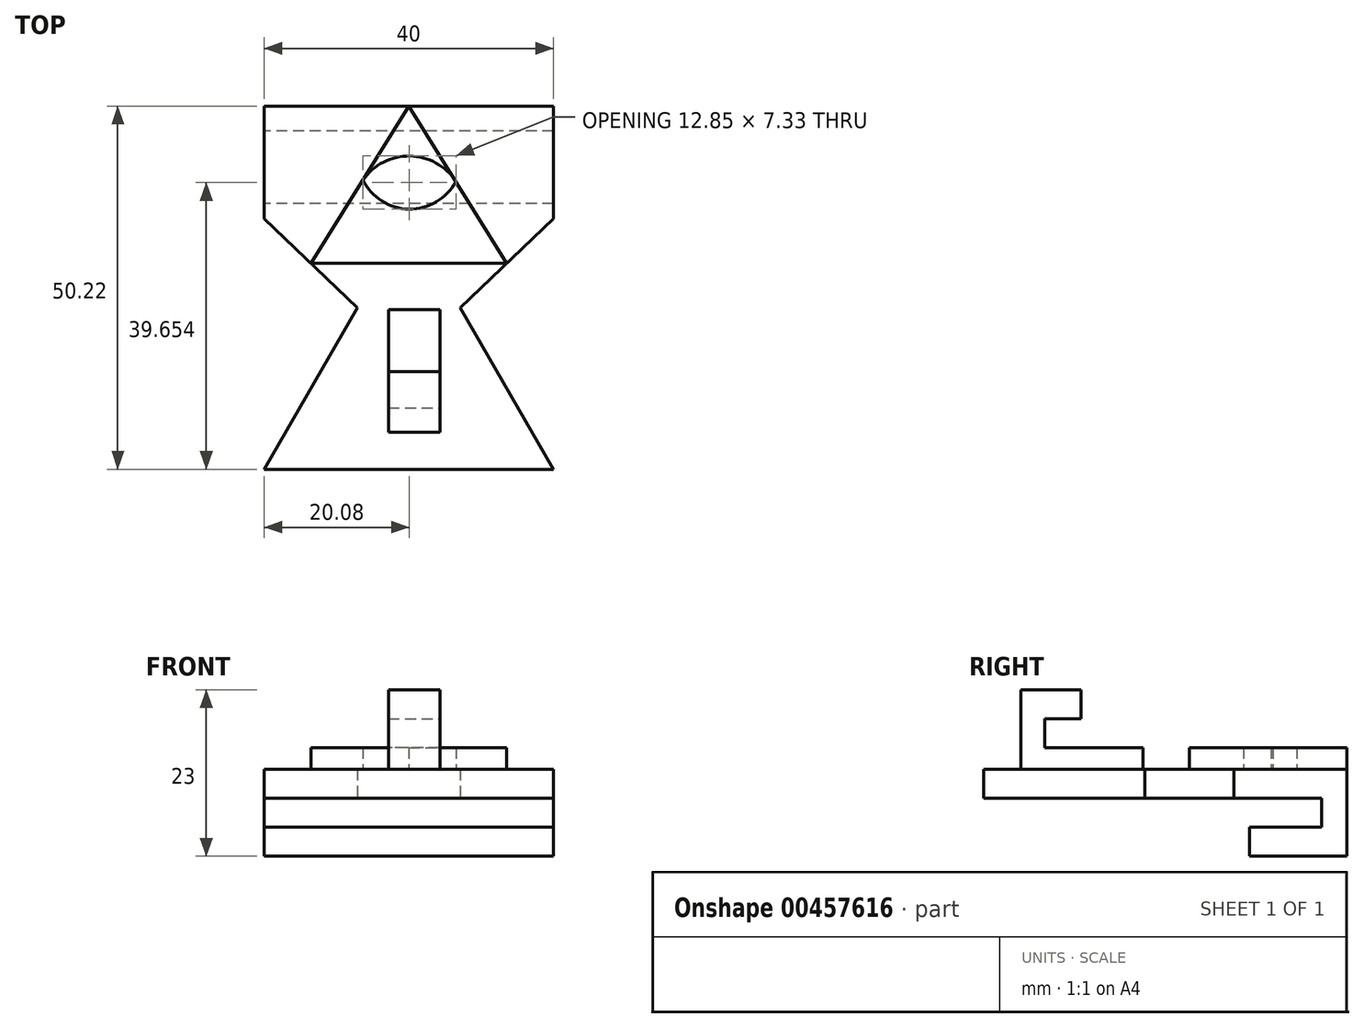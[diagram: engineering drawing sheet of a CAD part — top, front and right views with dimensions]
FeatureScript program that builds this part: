
annotation { "Feature Type Name" : "Feature", "Feature Type Description" : "" }
export const myFeature = defineFeature(function(context is Context, id is Id, definition is map)
    precondition{}
    {
        {
            var Q0;
            Q0=qCreatedBy(makeId("Top.planeOp"),FACE);
            var sketch = newSketch(context, id + "F0", { "sketchPlane" : qUnion([Q0])});
            skLineSegment(sketch, "E0", {"start": v(0, 0) * mm, "end": v(-40, 0) * mm});
            skLineSegment(sketch, "E1", {"start": v(-40, 0) * mm, "end": v(-27.1, 22.34) * mm});
            skLineSegment(sketch, "E2", {"start": v(-12.9, 22.34) * mm, "end": v(0, 0) * mm});
            skLineSegment(sketch, "E3.top", {"start": v(0, 50.22) * mm, "end": v(-40, 50.22) * mm});
            skLineSegment(sketch, "E3.left", {"start": v(0, 34.64) * mm, "end": v(0, 50.22) * mm});
            skLineSegment(sketch, "E3.right", {"start": v(-40, 34.64) * mm, "end": v(-40, 50.22) * mm});
            skLineSegment(sketch, "E4", {"start": v(0, 34.64) * mm, "end": v(-12.9, 22.34) * mm});
            skLineSegment(sketch, "E5", {"start": v(-40, 34.64) * mm, "end": v(-27.1, 22.34) * mm});
            skPoint(sketch, "E6.orphan", {"position": v(-20, 34.64) * mm});
            skSolve(sketch);
        }
        {
            var Q0;
            Q0 = qSketchRegion(id + "F0", true);
            extrude(context, id + "F1", {"entities" : qUnion([Q0]), "depth" : 4 * mm});
        }
        {
            var Q0;
            Q0=makeQuery(id+"F1.opExtrude","CAP_FACE",FACE,{"disambiguationData":[OSD([sQuery(id+"F0.wireOp",EDGE,"E0"),sQuery(id+"F0.wireOp",EDGE,"E1"),sQuery(id+"F0.wireOp",EDGE,"E2"),sQuery(id+"F0.wireOp",EDGE,"E3.top"),sQuery(id+"F0.wireOp",EDGE,"E3.left"),sQuery(id+"F0.wireOp",EDGE,"E3.right"),sQuery(id+"F0.wireOp",EDGE,"E4"),sQuery(id+"F0.wireOp",EDGE,"E5")])],"isStart":true});
            var sketch = newSketch(context, id + "F2", { "sketchPlane" : qUnion([Q0])});
            skLineSegment(sketch, "E7.bottom", {"start": v(0, -50.22) * mm, "end": v(-40, -50.22) * mm});
            skLineSegment(sketch, "E7.top", {"start": v(0, -46.76) * mm, "end": v(-40, -46.76) * mm});
            skLineSegment(sketch, "E7.left", {"start": v(0, -50.22) * mm, "end": v(0, -46.76) * mm});
            skLineSegment(sketch, "E7.right", {"start": v(-40, -50.22) * mm, "end": v(-40, -46.76) * mm});
            skSolve(sketch);
        }
        {
            var Q0;
            Q0=makeQuery(id+"F2.imprint","IMPRINT",FACE,{"disambiguationData":[TD([[makeQuery(id+"F2.imprint","IMPRINT",EDGE,{"derivedFrom":sQuery(id+"F2.wireOp",EDGE,"E7.bottom")}),-1.0]])]});
            extrude(context, id + "F3", {"entities" : qUnion([Q0]), "operationType" : NewBodyOperationType.ADD, "depth" : 8 * mm});
        }
        {
            var Q0;
            Q0=makeQuery(id+"F3.opExtrude","SWEPT_FACE",FACE,{"disambiguationData":[OSD([sQuery(id+"F2.wireOp",EDGE,"E7.top")])]});
            var sketch = newSketch(context, id + "F4", { "sketchPlane" : qUnion([Q0])});
            skLineSegment(sketch, "E8.bottom", {"start": v(-40, -8) * mm, "end": v(0, -8) * mm});
            skLineSegment(sketch, "E8.top", {"start": v(-40, -4) * mm, "end": v(0, -4) * mm});
            skLineSegment(sketch, "E8.left", {"start": v(-40, -8) * mm, "end": v(-40, -4) * mm});
            skLineSegment(sketch, "E8.right", {"start": v(0, -8) * mm, "end": v(0, -4) * mm});
            skSolve(sketch);
        }
        {
            var Q0;
            Q0=makeQuery(id+"F4.imprint","IMPRINT",FACE,{"disambiguationData":[TD([[makeQuery(id+"F4.imprint","IMPRINT",EDGE,{"derivedFrom":sQuery(id+"F4.wireOp",EDGE,"E8.bottom")}),-1.0]])]});
            extrude(context, id + "F5", {"entities" : qUnion([Q0]), "operationType" : NewBodyOperationType.ADD, "depth" : 10 * mm});
        }
        {
            var Q0;
            Q0=makeQuery(id+"F1.opExtrude","CAP_FACE",FACE,{"disambiguationData":[OSD([sQuery(id+"F0.wireOp",EDGE,"E0"),sQuery(id+"F0.wireOp",EDGE,"E1"),sQuery(id+"F0.wireOp",EDGE,"E2"),sQuery(id+"F0.wireOp",EDGE,"E3.top"),sQuery(id+"F0.wireOp",EDGE,"E3.left"),sQuery(id+"F0.wireOp",EDGE,"E3.right"),sQuery(id+"F0.wireOp",EDGE,"E4"),sQuery(id+"F0.wireOp",EDGE,"E5")])],"isStart":false});
            var sketch = newSketch(context, id + "F6", { "sketchPlane" : qUnion([Q0])});
            skLineSegment(sketch, "E9.bottom", {"start": v(-22.81, 22.08) * mm, "end": v(-15.7, 22.08) * mm});
            skLineSegment(sketch, "E9.top", {"start": v(-22.81, 5.15) * mm, "end": v(-15.7, 5.15) * mm});
            skLineSegment(sketch, "E9.left", {"start": v(-22.81, 22.08) * mm, "end": v(-22.81, 5.15) * mm});
            skLineSegment(sketch, "E9.right", {"start": v(-15.7, 22.08) * mm, "end": v(-15.7, 5.15) * mm});
            skSolve(sketch);
        }
        {
            var Q0;
            Q0=makeQuery(id+"F6.imprint","IMPRINT",FACE,{"disambiguationData":[TD([[makeQuery(id+"F6.imprint","IMPRINT",EDGE,{"derivedFrom":sQuery(id+"F6.wireOp",EDGE,"E9.bottom")}),-1.0]])]});
            extrude(context, id + "F7", {"entities" : qUnion([Q0]), "operationType" : NewBodyOperationType.ADD, "depth" : 3 * mm});
        }
        {
            var Q0;
            Q0=makeQuery(id+"F7.opExtrude","CAP_FACE",FACE,{"disambiguationData":[OSD([sQuery(id+"F6.wireOp",EDGE,"E9.bottom"),sQuery(id+"F6.wireOp",EDGE,"E9.top"),sQuery(id+"F6.wireOp",EDGE,"E9.left"),sQuery(id+"F6.wireOp",EDGE,"E9.right")])],"isStart":false});
            var sketch = newSketch(context, id + "F8", { "sketchPlane" : qUnion([Q0])});
            skLineSegment(sketch, "E10.bottom", {"start": v(-22.81, 5.15) * mm, "end": v(-15.7, 5.15) * mm});
            skLineSegment(sketch, "E10.top", {"start": v(-22.81, 8.48) * mm, "end": v(-15.7, 8.48) * mm});
            skLineSegment(sketch, "E10.left", {"start": v(-22.81, 5.15) * mm, "end": v(-22.81, 8.48) * mm});
            skLineSegment(sketch, "E10.right", {"start": v(-15.7, 5.15) * mm, "end": v(-15.7, 8.48) * mm});
            skSolve(sketch);
        }
        {
            var Q0;
            Q0=makeQuery(id+"F8.imprint","IMPRINT",FACE,{"disambiguationData":[TD([[makeQuery(id+"F8.imprint","IMPRINT",EDGE,{"derivedFrom":sQuery(id+"F8.wireOp",EDGE,"E10.bottom")}),1.0]])]});
            extrude(context, id + "F9", {"entities" : qUnion([Q0]), "operationType" : NewBodyOperationType.ADD, "depth" : 8 * mm});
        }
        {
            var Q0;
            Q0=makeQuery(id+"F9.opExtrude","SWEPT_FACE",FACE,{"disambiguationData":[OSD([sQuery(id+"F8.wireOp",EDGE,"E10.top")])]});
            var sketch = newSketch(context, id + "F10", { "sketchPlane" : qUnion([Q0])});
            skLineSegment(sketch, "E11.bottom", {"start": v(22.81, 15) * mm, "end": v(15.7, 15) * mm});
            skLineSegment(sketch, "E11.top", {"start": v(22.81, 11) * mm, "end": v(15.7, 11) * mm});
            skLineSegment(sketch, "E11.left", {"start": v(22.81, 15) * mm, "end": v(22.81, 11) * mm});
            skLineSegment(sketch, "E11.right", {"start": v(15.7, 15) * mm, "end": v(15.7, 11) * mm});
            skSolve(sketch);
        }
        {
            var Q0;
            Q0 = qSketchRegion(id + "F10", true);
            extrude(context, id + "F11", {"entities" : qUnion([Q0]), "operationType" : NewBodyOperationType.ADD, "depth" : 5 * mm});
        }
        {
            var Q0;
            Q0=makeQuery(id+"F1.opExtrude","CAP_FACE",FACE,{"disambiguationData":[OSD([sQuery(id+"F0.wireOp",EDGE,"E0"),sQuery(id+"F0.wireOp",EDGE,"E1"),sQuery(id+"F0.wireOp",EDGE,"E2"),sQuery(id+"F0.wireOp",EDGE,"E3.top"),sQuery(id+"F0.wireOp",EDGE,"E3.left"),sQuery(id+"F0.wireOp",EDGE,"E3.right"),sQuery(id+"F0.wireOp",EDGE,"E4"),sQuery(id+"F0.wireOp",EDGE,"E5")])],"isStart":false});
            var sketch = newSketch(context, id + "F12", { "sketchPlane" : qUnion([Q0])});
            skLineSegment(sketch, "E12", {"start": v(-26.44, 39.89) * mm, "end": v(-26.78, 39.35) * mm});
            skLineSegment(sketch, "E13", {"start": v(-13.22, 39.35) * mm, "end": v(-13.49, 39.78) * mm});
            skArc(sketch, "E14", {"start": v(-13.22, 39.35) * mm, "mid": v(-13.35, 39.57) * mm, "end": v(-13.49, 39.78) * mm});
            skArc(sketch, "E15.trimOffspring", {"start": v(-26.44, 39.88) * mm, "mid": v(-26.61, 39.62) * mm, "end": v(-26.78, 39.35) * mm});
            skPoint(sketch, "E16.orphan", {"position": v(-20, 50.22) * mm});
            skPoint(sketch, "E17.start.orphan", {"position": v(-33.55, 28.49) * mm});
            skPoint(sketch, "E18.center.orphan", {"position": v(-20, 39.35) * mm});
            skPoint(sketch, "E19.start.orphan", {"position": v(-6.45, 28.49) * mm});
            skLineSegment(sketch, "E20", {"start": v(-20, 50.22) * mm, "end": v(-33.55, 28.49) * mm});
            skLineSegment(sketch, "E21", {"start": v(-6.45, 28.49) * mm, "end": v(-33.55, 28.49) * mm});
            skLineSegment(sketch, "E22", {"start": v(-20, 50.22) * mm, "end": v(-6.45, 28.49) * mm});
            skArc(sketch, "E23", {"start": v(-13.5, 39.78) * mm, "mid": v(-19.86, 43.32) * mm, "end": v(-26.35, 40) * mm});
            skArc(sketch, "E24", {"start": v(-26.35, 40) * mm, "mid": v(-19.99, 35.99) * mm, "end": v(-13.5, 39.78) * mm});
            skCircle(sketch, "E25", {"center": v(-20, 39.35) * mm, "radius": 1.84 * mm});
            skSolve(sketch);
        }
        {
            var Q0;
            {var subQ5=sQuery(id+"F12.wireOp",EDGE,"E21");Q0=makeQuery(id+"F12.imprint","IMPRINT",FACE,{"disambiguationData":[TD([[makeQuery(id+"F12.imprint","IMPRINT",EDGE,{"derivedFrom":subQ5}),-1.0]])]});}
            var Q1;
            {var subQ1=sQuery(id+"F12.wireOp",EDGE,"E23");Q1=makeQuery(id+"F12.imprint","IMPRINT",FACE,{"disambiguationData":[TD([[makeQuery(id+"F12.imprint","IMPRINT",EDGE,{"derivedFrom":subQ1}),-1.0]])]});}
            extrude(context, id + "F13", {"entities" : qUnion([Q0, Q1]), "depth" : 3 * mm});
        }
    });
